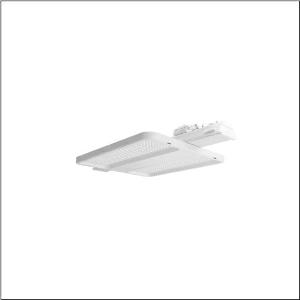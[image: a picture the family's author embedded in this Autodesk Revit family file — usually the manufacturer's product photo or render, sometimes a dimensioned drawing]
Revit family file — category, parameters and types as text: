
# Revit family: highbay_11_fur_licross_tragschiene_midi_51hn11da4mla02
name_source: partatom
category: Lighting Fixtures
units: mm (PartAtom-declared; Revit-internal decimal feet)

## family parameters
Cut with Voids When Loaded = No
Host = Face
Light Source = No
Part Type = Normal
Room Calculation Point = No
Round Connector Dimension = Use Diameter
Shared = No

## types (1)
- --- (1 x LED, 28000 lm, 147.1 W, 4000K)
    Apparent Load = 147 VA
    CIE Flux Codes = 85 97 100 100 100
    Color Rendering = 80
    Color Temperature = 4000K
    Default Elevation = 1800 mm
    Description = high bay luminaire Highbay 11 for Licross trunking rail midi; direct symmetric narrow distribution, light control with lens of PMMA; UGR ≤ 22 (X = 4H | Y = 8H | S = 0.25H | reflection values 70/50/20); luminous flux: 28.000lm; light colour: 840, colour temperature: 4000K, MacAdam ≤ 2 SDCM (initial), colour rendering: CRI > 80; luminous efficacy: 190,3lm/W; rated service life: 100.000h (L95) at AT= 25°C; control: Bluetooth Mesh; for wireless networking: Node luminaire for setting up a local control solution without a higher-level application controller, intelligence completely in the luminaire; no control line such as DALI between the Node multi-sensor luminaires and Nodes is required, wireless integration of other Node luminaires and Node multi-sensor luminaires into the network is possible; number of Node luminaires in the project can be expanded as required, network sizes > 300 Nodes can be realized; can also be connected to lighting or building automation via various gateways upon request; integrated DALI2 ECG provides luminaire data (according to IEC62386, Part 251), energy data (Part 252), and monitoring and analytics data (Part 253) to higher-level systems for further processing; luminaire connection: plug, 5-pole, with phase selectionmains connection: 230..240V, AC 50/60Hz; connected load: 147,1W; protection rating (complete): IP64; insulation class (complete): insulation class I (protective earthing); protection symbol: D; impact resistance: IK06; certification: CE, UKCA; internal wiring halogen-free; luminaire LABS conformity tested according to VDMA 24364:2018-05; Suitable for use in the food industry according to the specifications of IFS-Food, HACCP and/or BRC; housing frame of high-performance plastic PA6, matt traffic white (RAL 9016); cover of PMMA; fixing on rail side of steel, galvanised, white; blank cover of PC/ABS, traffic white (RAL 9016); dimension (LxWxH): 750 x 442 x 72mm; permissible operating ambient temperature: -20..+35°C (reducing of maximum allowable ambient temperature of 5°C with ceiling mounting); packaging unit: 1 piece
    Height = 72 mm  [stored 0.23622 ft]
    Lamp = 1 x LED
    Lamp Light Flux = 28000 lm
    Lamp Power = 147.1 W
    Lamp count = 1
    Length = 474 mm
    Luminous efficacy = 190 lm/W
    Manufacturer = Siteco
    ModVariant = No
    Model = 51HN11DA4MLA02
    Mounting Place = Ceiling
    Mounting Type = Pendant
    Number of Poles = 1
    OnlyDefault = Yes
    Power Factor = 1
    Product Name = Highbay 11 für Licross Tragschiene midi
    Product group = high bay luminaire
    ProductGroupID = 902
    Protection Class = Protection class I
    Protection Degree = IP 64
    RLX_Detail_Level = 1
    RLX_Emergency_Light_Flux = 0 lm
    RLX_Emergency_Type = 0
    RLX_Emergency_Type_DB = No
    RlxData = <blob elided: 18065 chars, md5=e6b019c8>
    Socket = socket
    Standby Power = 0 W
    System Light Flux = 28000 lm
    System Power = 147 W
    Type Comments = factory setting: luminous flux: 100 % | dim-lin: 254 | 661 mA
    Type Image = l_1363258.jpg
    URL = http://relux.com
    VarID = @adj_025217
    Voltage = 0 V
    Weight = 0.00 kg
    Width = 442 mm

note: [stored X ft] marks values corroborated as IEEE doubles in the binary element streams (Revit-internal decimal feet)

## geometry (parser evidence)
native form markers: Blend x4, Sweep x12
no freeform markers — native parametric forms only
